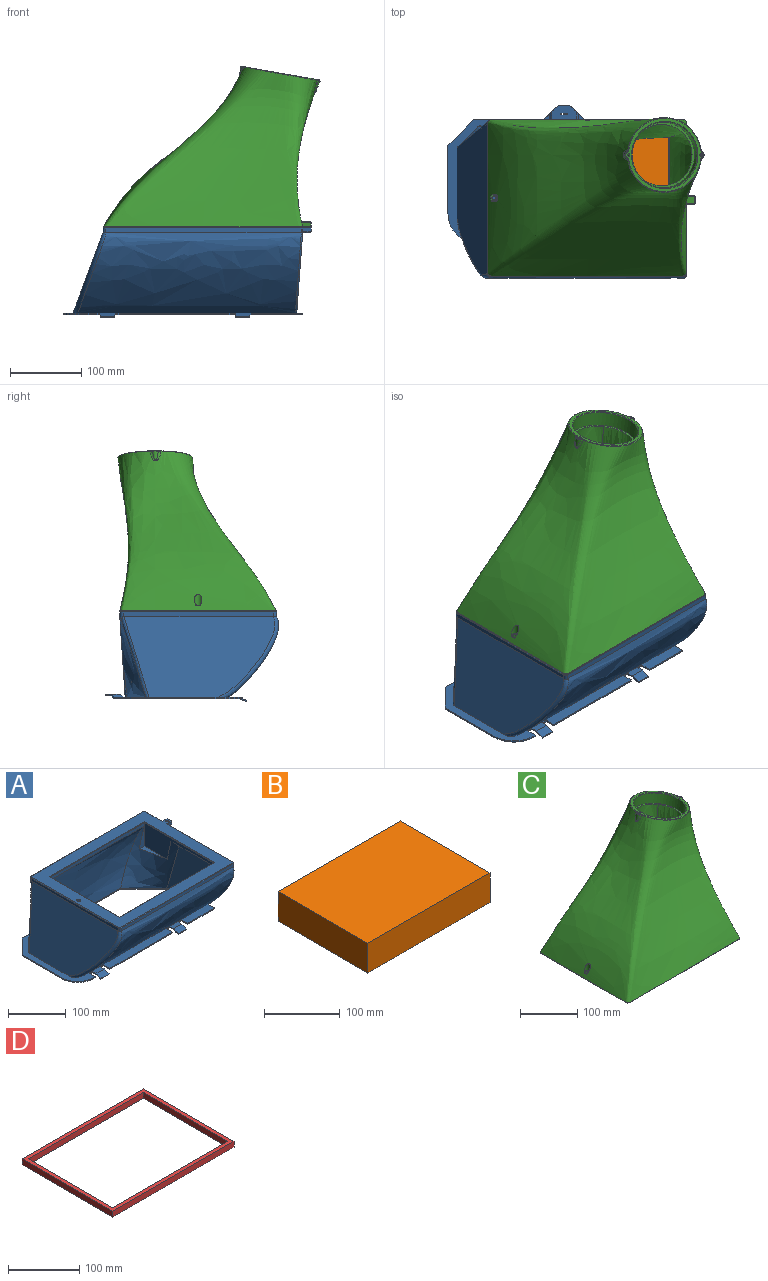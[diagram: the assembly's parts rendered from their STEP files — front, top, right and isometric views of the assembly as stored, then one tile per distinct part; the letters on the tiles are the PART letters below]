
ASSEMBLY  parts=4 mates=3
PART A: 123 faces, bbox 348.3x257.9x147.8 mm
  f0: plane 40x6.5mm, normal (1,0,0), area 254mm2, adj f71,f85,f99,f102,f113
  f1: bspline ~113x103.13mm, area 7040.3mm2, adj f57,f65,f77,f78,f93,f94,f120
  f2: plane 211.11x6.83mm, normal (-1,0,0), area 1371.6mm2, adj f74,f83,f86,f91,f92,f106
  f3: plane 335.43x180.15mm, normal (0,0,1), area 10633.3mm2, adj f5,f6,f7,f8,f9,f10,f11,f12
  f4: plane 39.82x4mm, normal (0,1,0), area 144.2mm2, adj f25,f36,f37,f41
  f5: plane 96.43x2mm, normal (0,1,0), area 192.9mm2, adj f3,f25,f33,f49
  f6: plane 21.22x6.32mm, normal (1,0,0), area 42.5mm2, adj f3,f7,f25,f29,f30,f31
  f7: plane 8x2mm, normal (0,-1,0), area 16mm2, adj f3,f6,f8,f25
  f8: plane 15x2mm, normal (-1,0,0), area 30mm2, adj f3,f7,f9,f25
  f9: plane 154x2mm, normal (0,-1,0), area 308mm2, adj f3,f8,f10,f25
  f10: plane 15x2mm, normal (1,0,0), area 30mm2, adj f3,f9,f11,f25
  f11: plane 8x2mm, normal (0,-1,0), area 16mm2, adj f3,f10,f12,f25
  f12: plane 21.22x6.32mm, normal (-1,0,0), area 42.5mm2, adj f3,f11,f25,f26,f27,f28
  f13: plane 21.22x6.32mm, normal (1,0,0), area 42.5mm2, adj f3,f14,f25,f26,f27,f28
  f14: plane 8x2mm, normal (0,-1,0), area 16mm2, adj f3,f13,f15,f25
  f15: plane 15x2mm, normal (-1,0,0), area 30mm2, adj f3,f14,f16,f25
  f16: plane 66x2mm, normal (0,-1,0), area 132mm2, adj f3,f15,f17,f25
  f17: plane 86.29x2mm, normal (1,0,0), area 172.6mm2, adj f3,f16,f25,f34
  f18: plane 55.72x2mm, normal (0,1,0), area 111.4mm2, adj f3,f25,f35,f50
  f19: plane 96x2mm, normal (-1,0,0), area 192mm2, adj f3,f20,f25,f33
  f20: cylinder r=40mm len=40mm, axis (0,0,-1), area 125.7mm2, adj f3,f19,f21,f25
  f21: plane 3x2mm, normal (0,-1,0), area 6mm2, adj f3,f20,f22,f25
  f22: plane 15x2mm, normal (1,0,0), area 30mm2, adj f3,f21,f23,f25
  f23: plane 8x2mm, normal (0,-1,0), area 16mm2, adj f3,f22,f24,f25
  f24: plane 21.22x6.32mm, normal (-1,0,0), area 42.5mm2, adj f3,f23,f25,f29,f30,f31
  f25: plane 335x180.59mm, normal (0,0,-1), area 19028.8mm2, adj f4,f5,f6,f7,f8,f9,f10,f11
  f26: plane 20x11.51mm, normal (0,0.35,-0.94), area 245.9mm2, adj f12,f13,f25,f28
  f27: plane 20x12.22mm, normal (0,-0.34,0.94), area 260mm2, adj f3,f12,f13,f28
  f28: plane 20x1.87mm, normal (0,-0.94,-0.35), area 40mm2, adj f12,f13,f26,f27
  f29: plane 20x11.51mm, normal (0,0.35,-0.94), area 245.9mm2, adj f6,f24,f25,f31
  f30: plane 20x12.22mm, normal (0,-0.34,0.94), area 260mm2, adj f3,f6,f24,f31
  f31: plane 20x1.87mm, normal (0,-0.94,-0.35), area 40mm2, adj f6,f24,f29,f30
  f32: plane 35.71x35.71mm, normal (0.71,0.71,0), area 101mm2, adj f3,f25,f34,f35
  f33: plane 36x36mm, normal (-0.71,0.71,0), area 101.8mm2, adj f3,f5,f19,f25
  f34: cylinder r=50mm len=35.36mm, axis (0,0,1), area 78.5mm2, adj f3,f17,f25,f32
  f35: cylinder r=50mm len=35.36mm, axis (0,0,-1), area 78.5mm2, adj f3,f18,f25,f32
  f36: plane 32.28x20mm, normal (0,0,-1), area 564.9mm2, adj f4,f37,f41,f42,f43,f44,f45,f46
  f37: plane 12.36x4mm, normal (-0.73,0,-0.69), area 57.6mm2, adj f4,f25,f36,f48
  f38: plane 16.5x4mm, normal (0.73,0,0.69), area 69.4mm2, adj f3,f39,f48,f59
  f39: plane 34x21mm, normal (0,0,1), area 619.4mm2, adj f38,f40,f42,f43,f44,f45,f46,f47
  f40: plane 16.5x4mm, normal (-0.73,0,0.69), area 69.4mm2, adj f3,f39,f47,f59
  f41: plane 12.36x4mm, normal (0.73,0,-0.69), area 57.6mm2, adj f4,f25,f36,f47
  f42: plane 8.72x2mm, normal (0,1,0), area 17.4mm2, adj f36,f39,f51,f52
  f43: plane 9x2mm, normal (0,1,0), area 18mm2, adj f36,f39,f44,f46
  f44: plane 2x2mm, normal (-1,0,0), area 4mm2, adj f36,f39,f43,f45
  f45: plane 9x2mm, normal (0,-1,0), area 18mm2, adj f36,f39,f44,f46
  f46: plane 2x2mm, normal (1,0,0), area 4mm2, adj f36,f39,f43,f45
  f47: plane 15.61x15.61mm, normal (-0.71,0.71,0), area 49mm2, adj f3,f25,f36,f39,f40,f41,f49,f51
  f48: plane 15.61x15.61mm, normal (0.71,0.71,0), area 49mm2, adj f3,f25,f36,f37,f38,f39,f50,f52
  f49: cylinder r=5mm len=3.54mm, axis (0,0,-1), area 7.9mm2, adj f3,f5,f25,f47
  f50: cylinder r=5mm len=3.54mm, axis (0,0,1), area 7.9mm2, adj f3,f18,f25,f48
  f51: cylinder r=10mm len=7.07mm, axis (0,0,-1), area 15.7mm2, adj f36,f39,f42,f47
  f52: cylinder r=10mm len=7.07mm, axis (0,0,1), area 15.7mm2, adj f36,f39,f42,f48
  f53: plane 26.89x26.74mm, normal (0.71,-0.71,0), area 75.9mm2, adj f25,f54,f58,f81
  f54: plane 95.91x2mm, normal (1,0,0), area 191.8mm2, adj f25,f53,f55,f80
  f55: plane 298.87x2mm, normal (0,1,0), area 597.7mm2, adj f25,f54,f56,f79
  f56: plane 65.27x2mm, normal (-1,0,0), area 130.5mm2, adj f25,f55,f78,f120
  f57: plane 56.12x56.12mm, normal (-0.71,-0.71,0), area 158.7mm2, adj f1,f25,f58,f120
  f58: plane 215.41x2mm, normal (0,-1,0), area 430.8mm2, adj f25,f53,f57,f77
  f59: plane 41.55x4mm, normal (0,-0.71,0.71), area 213.7mm2, adj f3,f38,f39,f40
  f60: plane 163x6.5mm, normal (1,0,0), area 1053.5mm2, adj f71,f72,f98,f100,f105,f122
  f61: plane 270.09x6.59mm, normal (0,1,0), area 1754.9mm2, adj f75,f76,f85,f91,f95,f110
  f62: plane 0.31x0.1mm, normal (-1,0,0), area 0mm2, adj f75,f83,f91
  f63: plane 170x6.5mm, normal (1,0,0), area 1105mm2, adj f64,f66,f80,f81,f88
  f64: plane 230x6.5mm, normal (0,-1,0), area 1495mm2, adj f63,f65,f77,f90
  f65: plane 170x49mm, normal (-1,0,0), area 3704.9mm2, adj f1,f64,f66,f78,f89,f93,f94
  f66: plane 230x6.5mm, normal (0,1,0), area 1495mm2, adj f63,f65,f79,f87
  f67: cylinder r=2.4mm len=6.5mm, axis (0,0,-1), area 98mm2, adj f70,f118
  f68: plane 274.01x6.55mm, normal (0,-1,0), area 1781mm2, adj f73,f86,f92,f103,f122
  f69: plane 290x218mm, normal (0,0,1), area 20420.7mm2, adj f103,f104,f105,f106,f107,f108,f109,f110
  f70: plane 4.8x4.8mm, normal (0,0,1), area 18.1mm2, adj f67
  f71: bspline ~113x110mm, area 10507.5mm2, adj f0,f3,f60,f84,f85,f95,f96
  f72: plane 151.2x114.28mm, normal (1,0,-0.07), area 12117.5mm2, adj f3,f60,f84,f121,f122
  f73: bspline ~322.28x113mm, area 40414.6mm2, adj f3,f68,f86,f121
  f74: plane 211.95x113.01mm, normal (-0.94,0,0.35), area 20318.5mm2, adj f2,f3,f83,f86
  f75: bspline ~182.28x113mm, area 9518mm2, adj f3,f61,f62,f82,f83,f91
  f76: plane 280.98x113.04mm, normal (0,1,-0.07), area 19834.7mm2, adj f3,f61,f82,f95
  f77: bspline ~263.04x113mm, area 25595.8mm2, adj f1,f58,f64,f81
  f78: plane 143.21x113.44mm, normal (-1,0,-0.08), area 10737.4mm2, adj f1,f56,f65,f79,f120
  f79: bspline ~298.87x113mm, area 37651.6mm2, adj f55,f66,f78,f80
  f80: plane 172.95x113mm, normal (0.88,0,-0.47), area 13864mm2, adj f54,f63,f79,f81
  f81: bspline ~113x94.83mm, area 7364mm2, adj f53,f63,f77,f80
  f82: bspline ~164.07x124.8mm, area 243.4mm2, adj f3,f75,f76
  f83: bspline ~134.12x54.71mm, area 842mm2, adj f2,f3,f62,f74,f75,f91
  f84: bspline ~122.58x45.85mm, area 155.3mm2, adj f3,f71,f72
  f85: cylinder r=5mm len=6.53mm, axis (0,0,-1), area 49.6mm2, adj f0,f61,f71,f95,f112
  f86: bspline ~130.13x100.4mm, area 1286.7mm2, adj f2,f3,f68,f73,f74,f92
  f87: plane 231.41x0.71mm, normal (0,0.71,0.71), area 230.7mm2, adj f66,f88,f89,f116
  f88: plane 171.41x0.71mm, normal (0.71,0,0.71), area 170.7mm2, adj f63,f87,f90,f114
  f89: plane 171.41x0.71mm, normal (-0.71,0,0.71), area 170.7mm2, adj f65,f87,f90,f117
  f90: plane 231.41x0.71mm, normal (0,-0.71,0.71), area 230.7mm2, adj f64,f88,f89,f115
  f91: cylinder r=5mm len=21.54mm, axis (0,0,-1), area 73.1mm2, adj f2,f61,f62,f75,f83,f108
  f92: cylinder r=4mm len=6.61mm, axis (0,0,-1), area 41.3mm2, adj f2,f68,f86,f104
  f93: plane 42.5x12.33mm, normal (0,-1,0), area 263.7mm2, adj f1,f65,f94
  f94: plane 57.12x13.2mm, normal (0,0,1), area 320.2mm2, adj f1,f65,f93
  f95: bspline ~140.44x86.16mm, area 804.5mm2, adj f3,f61,f71,f76,f85
  f96: plane 11x10mm, normal (0,0,-1), area 91.1mm2, adj f71,f100,f101,f102,f119
  f97: plane 12x5.5mm, normal (1,0,0), area 66mm2, adj f98,f99,f101,f109
  f98: plane 12x5.5mm, normal (0,-1,0), area 66mm2, adj f60,f97,f100,f107
  f99: plane 12x5.5mm, normal (0,1,0), area 66mm2, adj f0,f97,f102,f111
  f100: plane 12x1mm, normal (0,-0.71,-0.71), area 16.3mm2, adj f60,f96,f98,f101
  f101: plane 12x1mm, normal (0.71,0,-0.71), area 15.6mm2, adj f96,f97,f100,f102
  f102: plane 12x1mm, normal (0,0.71,-0.71), area 16.3mm2, adj f0,f96,f99,f101
  f103: plane 275x1mm, normal (0,-0.71,0.71), area 388.2mm2, adj f68,f69,f104,f122
  f104: cone r=3mm half-angle=45deg, axis (0,0,-1), area 7.8mm2, adj f69,f92,f103,f106
  f105: plane 164x1mm, normal (0.71,0,0.71), area 230.5mm2, adj f60,f69,f107,f122
  f106: plane 211x1mm, normal (-0.71,0,0.71), area 298.4mm2, adj f2,f69,f104,f108
  f107: plane 13x1mm, normal (0,-0.71,0.71), area 17mm2, adj f69,f98,f105,f109
  f108: cone r=4mm half-angle=45deg, axis (0,0,-1), area 10mm2, adj f69,f91,f106,f110
  f109: plane 12x1mm, normal (0.71,0,0.71), area 15.6mm2, adj f69,f97,f107,f111
  f110: plane 270x1mm, normal (0,0.71,0.71), area 381.8mm2, adj f61,f69,f108,f112
  f111: plane 13x1mm, normal (0,0.71,0.71), area 17mm2, adj f69,f99,f109,f113
  f112: cone r=4mm half-angle=45deg, axis (0,0,-1), area 10mm2, adj f69,f85,f110,f113
  f113: plane 40x1mm, normal (0.71,0,0.71), area 55.9mm2, adj f0,f69,f111,f112
  f114: plane 172.83x0.71mm, normal (0.38,0,0.92), area 131.7mm2, adj f69,f88,f115,f116
  f115: plane 232.83x0.71mm, normal (0,-0.38,0.92), area 177.7mm2, adj f69,f90,f114,f117
  f116: plane 232.83x0.71mm, normal (0,0.38,0.92), area 177.7mm2, adj f69,f87,f114,f117
  f117: plane 172.83x0.71mm, normal (-0.38,0,0.92), area 131.7mm2, adj f69,f89,f115,f116
  f118: cone r=2.4mm half-angle=45deg, axis (0,0,1), area 25.8mm2, adj f67,f69
  f119: cylinder r=2.45mm len=7.5mm, axis (0,0,-1), area 115.5mm2, adj f69,f96
  f120: cylinder r=2mm len=2.89mm, axis (0,0,1), area 3.8mm2, adj f1,f25,f56,f57,f78
  f121: bspline ~117.53x77.92mm, area 374.4mm2, adj f3,f72,f73,f122
  f122: plane 8.07x2.01mm, normal (0.71,-0.71,0), area 20.6mm2, adj f60,f68,f72,f103,f105,f121
PART B: 6 faces, bbox 228x168x48 mm
  f0: plane 168x48mm, normal (1,0,0), area 8064mm2, adj f1,f3,f4,f5
  f1: plane 228x48mm, normal (0,1,0), area 10944mm2, adj f0,f2,f4,f5
  f2: plane 168x48mm, normal (-1,0,0), area 8064mm2, adj f1,f3,f4,f5
  f3: plane 228x48mm, normal (0,-1,0), area 10944mm2, adj f0,f2,f4,f5
  f4: plane 228x168mm, normal (0,0,-1), area 38304mm2, adj f0,f1,f2,f3
  f5: plane 228x168mm, normal (0,0,1), area 38304mm2, adj f0,f1,f2,f3
PART C: 83 faces, bbox 305.1x223.2x230.5 mm
  f0: bspline ~300.89x225.23mm, area 152443.7mm2, adj f1,f2,f18,f20,f21,f22,f27,f29
  f1: bspline ~89.35x0.79mm, area 54.6mm2, adj f0,f4,f56,f71
  f2: bspline ~137.51x0.79mm, area 90.6mm2, adj f0,f4,f53,f76
  f3: cylinder r=3.25mm len=8mm, axis (0,0,-1), area 163.4mm2, adj f4,f66
  f4: plane 290.02x218.33mm, normal (0,0,-1), area 17024.7mm2, adj f1,f2,f3,f46,f47,f48,f49,f50
  f5: plane 109.43x103.34mm, normal (0.17,0,0.98), area 1397.8mm2, adj f23,f25,f27,f28,f29,f30,f31,f32
  f6: cylinder r=46.25mm len=94.65mm, axis (0.17,0,0.98), area 5957.2mm2, adj f7,f45
  f7: plane 93.25x91.84mm, normal (0.17,0,0.98), area 847.3mm2, adj f6,f13,f14,f15,f16
  f8: plane 240x9.42mm, normal (0,-1,0), area 2259.9mm2, adj f9,f11,f12,f58
  f9: plane 180x9.42mm, normal (1,0,0), area 1694.9mm2, adj f8,f10,f12,f57
  f10: plane 240x9.42mm, normal (0,1,0), area 2259.9mm2, adj f9,f11,f12,f59
  f11: plane 180x9.42mm, normal (-1,0,0), area 1694.9mm2, adj f8,f10,f12,f60
  f12: plane 240.04x180.04mm, normal (0,0,-1), area 7629.7mm2, adj f8,f9,f10,f11,f61,f62,f63,f64
  f13: bspline ~251.14x202.89mm, area 32000.9mm2, adj f7,f14,f16,f61,f63
  f14: bspline ~203.9x184.18mm, area 26734.7mm2, adj f7,f13,f15,f62,f63,f64
  f15: bspline ~240.4x194.91mm, area 28131.2mm2, adj f7,f14,f16,f61,f62
  f16: bspline ~180.91x168.76mm, area 20640.8mm2, adj f7,f13,f15,f61
  f17: cylinder r=5mm len=13.11mm, axis (0.17,0,0.98), area 80.9mm2, adj f18,f41
  f18: bspline ~18.38x16.23mm, area 95.4mm2, adj f0,f17,f39,f43
  f19: cone r=5mm half-angle=12deg, axis (0.17,0,0.98), area 91.1mm2, adj f20,f21,f22,f30
  f20: plane 6.45x1.16mm, normal (-0.17,0,-0.98), area 2.3mm2, adj f0,f19,f21,f22
  f21: bspline ~24.7x8.01mm, area 77.8mm2, adj f0,f19,f20,f28
  f22: bspline ~23.63x7.79mm, area 77mm2, adj f0,f19,f20,f32
  f23: cylinder r=1.65mm len=15.35mm, axis (0.17,0,0.98), area 155.5mm2, adj f5,f24
  f24: plane 3.3x3.25mm, normal (0.17,0,0.98), area 8.6mm2, adj f23
  f25: cylinder r=1.65mm len=15.35mm, axis (0.17,0,0.98), area 155.5mm2, adj f5,f26
  f26: plane 3.3x3.25mm, normal (0.17,0,0.98), area 8.6mm2, adj f25
  f27: bspline ~18.88x6.89mm, area 26.9mm2, adj f0,f5,f28,f29
  f28: bspline ~4.45x2.96mm, area 7.2mm2, adj f5,f21,f27,f30
  f29: bspline ~19.77x19.31mm, area 34.5mm2, adj f0,f5,f27,f31
  f30: cone r=3.77mm half-angle=39deg, axis (-0.17,0,-0.98), area 13mm2, adj f5,f19,f28,f32
  f31: bspline ~25.97x7.65mm, area 37.8mm2, adj f0,f5,f29,f33
  f32: bspline ~4.42x2.95mm, area 7.2mm2, adj f5,f22,f30,f34
  f33: bspline ~26.08x7.57mm, area 35.8mm2, adj f0,f5,f31,f35
  f34: bspline ~18.85x6.99mm, area 28mm2, adj f0,f5,f32,f36
  f35: bspline ~19.75x19.6mm, area 30.1mm2, adj f0,f5,f33,f37
  f36: bspline ~19.75x19.24mm, area 37.6mm2, adj f0,f5,f34,f38
  f37: bspline ~18.79x7.24mm, area 22.5mm2, adj f0,f5,f35,f39
  f38: bspline ~25.89x7.82mm, area 38.6mm2, adj f0,f5,f36,f40
  f39: bspline ~4.49x3.39mm, area 6.4mm2, adj f5,f18,f37,f41
  f40: bspline ~26.07x7.71mm, area 36.5mm2, adj f0,f5,f38,f42
  f41: cone r=4mm half-angle=45deg, axis (-0.17,0,-0.98), area 12mm2, adj f5,f17,f39,f43
  f42: bspline ~19.75x19.62mm, area 33mm2, adj f0,f5,f40,f44
  f43: bspline ~4.47x3.39mm, area 6.3mm2, adj f5,f18,f41,f44
  f44: bspline ~18.79x7.32mm, area 23.7mm2, adj f0,f5,f42,f43
  f45: cone r=46.25mm half-angle=45deg, axis (0.17,0,0.98), area 415.4mm2, adj f5,f6
  f46: bspline ~165x0.93mm, area 167.7mm2, adj f0,f4,f47,f48
  f47: bspline ~4.56x4.41mm, area 6.7mm2, adj f0,f4,f46,f49
  f48: bspline ~45x0.9mm, area 45.5mm2, adj f0,f4,f46,f50
  f49: bspline ~135x0.89mm, area 136.2mm2, adj f0,f4,f47,f51
  f50: bspline ~4.79x4.49mm, area 6.8mm2, adj f0,f4,f48,f52
  f51: bspline ~135x0.89mm, area 137mm2, adj f0,f4,f49,f53
  f52: bspline ~135x0.9mm, area 134.1mm2, adj f0,f4,f50,f54
  f53: bspline ~4.83x4.56mm, area 6.8mm2, adj f0,f2,f4,f51
  f54: bspline ~135x0.9mm, area 135mm2, adj f0,f4,f52,f55
  f55: bspline ~4.78x4.78mm, area 6.7mm2, adj f0,f4,f54,f56
  f56: bspline ~45x0.78mm, area 42.6mm2, adj f0,f1,f4,f55
  f57: plane 181.17x0.58mm, normal (0.71,0,-0.71), area 149.1mm2, adj f4,f9,f58,f59
  f58: plane 241.17x0.58mm, normal (0,-0.71,-0.71), area 198.6mm2, adj f4,f8,f57,f60
  f59: plane 241.17x0.58mm, normal (0,0.71,-0.71), area 198.6mm2, adj f4,f10,f57,f60
  f60: plane 181.17x0.58mm, normal (-0.71,0,-0.71), area 149.1mm2, adj f4,f11,f58,f59
  f61: bspline ~181.41x1.37mm, area 141.8mm2, adj f12,f13,f15,f16,f62,f63
  f62: bspline ~222.51x6.2mm, area 169.9mm2, adj f12,f14,f15,f61,f64
  f63: bspline ~244.76x2.2mm, area 129.4mm2, adj f12,f13,f14,f61,f64
  f64: bspline ~164.31x0.77mm, area 78.4mm2, adj f12,f14,f62,f63
  f65: cylinder r=5.25mm len=15.89mm, axis (0,0,1), area 261.9mm2, adj f0,f66
  f66: plane 10.5x10.33mm, normal (0,0,1), area 53.1mm2, adj f0,f3,f65
  f67: plane 10x5.5mm, normal (1,0,0), area 55mm2, adj f74,f75,f79,f80
  f68: plane 13.21x5.56mm, normal (0.02,1,0), area 67.4mm2, adj f0,f71,f73,f74
  f69: plane 13.14x5.56mm, normal (-0.02,-1,0), area 67.1mm2, adj f0,f76,f80,f82
  f70: plane 13.48x10.27mm, normal (0,0,1), area 134.3mm2, adj f0,f73,f79,f82
  f71: plane 11.83x1.2mm, normal (0.01,0.71,-0.71), area 16.3mm2, adj f0,f1,f4,f68,f72
  f72: plane 1x1mm, normal (0.58,0.57,-0.58), area 0.9mm2, adj f71,f74,f75
  f73: plane 13.47x1.23mm, normal (0.01,0.71,0.71), area 18.8mm2, adj f0,f68,f70,f77
  f74: plane 5.5x1mm, normal (0.71,0.7,0), area 7.7mm2, adj f67,f68,f72,f77
  f75: plane 10x1mm, normal (0.71,0,-0.71), area 14.1mm2, adj f4,f67,f72,f78
  f76: plane 11.81x1.21mm, normal (-0.01,-0.71,-0.71), area 16.2mm2, adj f0,f2,f4,f69,f78
  f77: plane 1x1mm, normal (0.58,0.57,0.58), area 0.9mm2, adj f73,f74,f79
  f78: plane 1.02x1mm, normal (0.57,-0.58,-0.57), area 0.9mm2, adj f75,f76,f80
  f79: plane 10x1mm, normal (0.71,0,0.71), area 14.1mm2, adj f67,f70,f77,f81
  f80: plane 5.5x1.02mm, normal (0.7,-0.71,0), area 7.8mm2, adj f67,f69,f78,f81
  f81: plane 1.02x1mm, normal (0.57,-0.58,0.57), area 0.9mm2, adj f79,f80,f82
  f82: plane 13.41x1.24mm, normal (-0.01,-0.71,0.71), area 18.7mm2, adj f0,f69,f70,f81
PART D: 10 faces, bbox 240x180x10 mm
  f0: plane 240x10mm, normal (0,-1,0), area 2400mm2, adj f1,f7,f8,f9
  f1: plane 180x10mm, normal (1,0,0), area 1800mm2, adj f0,f2,f8,f9
  f2: plane 240x10mm, normal (0,1,0), area 2400mm2, adj f1,f7,f8,f9
  f3: plane 228x10mm, normal (0,-1,0), area 2280mm2, adj f4,f6,f8,f9
  f4: plane 168x10mm, normal (-1,0,0), area 1680mm2, adj f3,f5,f8,f9
  f5: plane 228x10mm, normal (0,1,0), area 2280mm2, adj f4,f6,f8,f9
  f6: plane 168x10mm, normal (1,0,0), area 1680mm2, adj f3,f5,f8,f9
  f7: plane 180x10mm, normal (-1,0,0), area 1800mm2, adj f0,f2,f8,f9
  f8: plane 240x180mm, normal (0,0,1), area 4896mm2, adj f0,f1,f2,f3,f4,f5,f6,f7
  f9: plane 240x180mm, normal (0,0,-1), area 4896mm2, adj f0,f1,f2,f3,f4,f5,f6,f7
PLACE A t=(-6.17,-1.65,-0.63)mm fixed
PLACE B t=(22.29,-25.38,121.87)mm
PLACE C t=(-6.17,-1.65,-1.13)mm
PLACE D t=(22.29,-25.38,121.87)mm
MATE fastened A.f69 <-> D.f9  axis (0,0,1) through (22.29,-25.38,121.87)mm
MATE fastened B.f5 <-> A.f69  axis (0,0,1) through (22.29,-25.38,121.87)mm
MATE fastened A.f67 <-> C.f3  axis (0,0,1) through (-108.83,-25.65,121.87)mm
